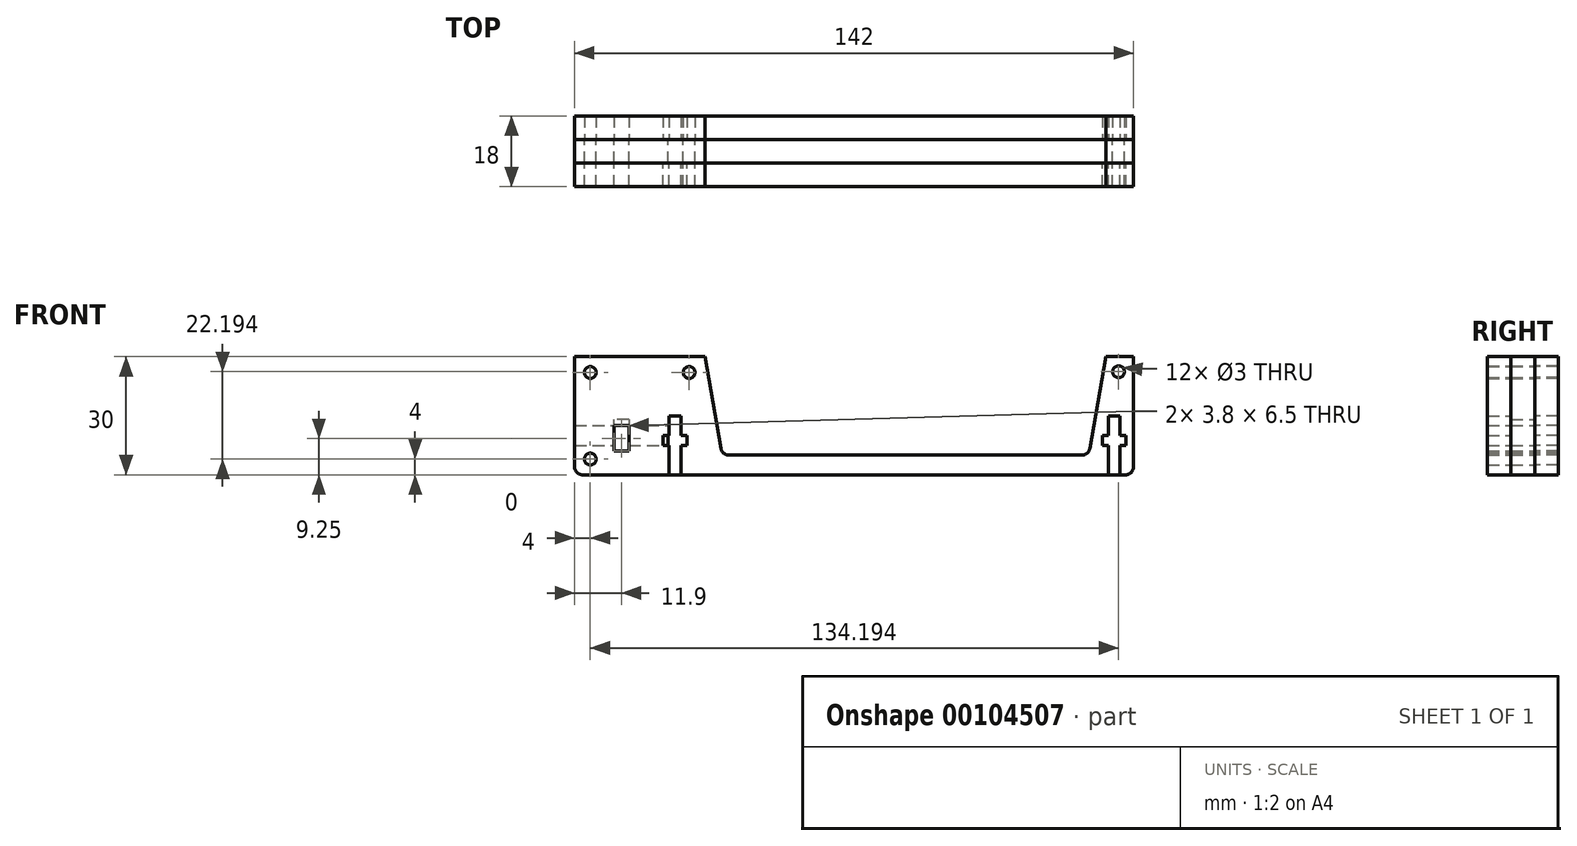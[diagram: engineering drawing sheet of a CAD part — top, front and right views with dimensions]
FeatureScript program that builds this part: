
annotation { "Feature Type Name" : "Feature", "Feature Type Description" : "" }
export const myFeature = defineFeature(function(context is Context, id is Id, definition is map)
    precondition{}
    {
        {
            var Q0;
            Q0=qCreatedBy(makeId("Front.planeOp"),FACE);
            var sketch = newSketch(context, id + "F0", { "sketchPlane" : qUnion([Q0])});
            skLineSegment(sketch, "E0", {"start": v(0, 2) * mm, "end": v(0, 7.5) * mm});
            skLineSegment(sketch, "E1", {"start": v(0, 30) * mm, "end": v(33.1, 30) * mm});
            skLineSegment(sketch, "E2", {"start": v(33.1, 30) * mm, "end": v(37.21, 6.65) * mm});
            skLineSegment(sketch, "E3", {"start": v(39.18, 5) * mm, "end": v(128.91, 5) * mm});
            skLineSegment(sketch, "E4", {"start": v(130.88, 6.65) * mm, "end": v(135, 30) * mm});
            skLineSegment(sketch, "E5", {"start": v(135, 30) * mm, "end": v(142, 30) * mm});
            skLineSegment(sketch, "E6", {"start": v(142, 30) * mm, "end": v(142, 2) * mm});
            skLineSegment(sketch, "E7", {"start": v(140, 0) * mm, "end": v(2, 0) * mm});
            skLineSegment(sketch, "E8", {"start": v(0, 10) * mm, "end": v(142, 10) * mm, "construction": true});
            skLineSegment(sketch, "E9", {"start": v(84.05, 0) * mm, "end": v(84.05, 5) * mm, "construction": true});
            skLineSegment(sketch, "E10.bottom", {"start": v(0, 12.5) * mm, "end": v(10, 12.5) * mm});
            skLineSegment(sketch, "E11.top", {"start": v(13.8, 14) * mm, "end": v(10, 14) * mm});
            skLineSegment(sketch, "E11.right", {"start": v(10, 12.5) * mm, "end": v(10, 14) * mm});
            skLineSegment(sketch, "E12", {"start": v(13.8, 14) * mm, "end": v(13.8, 12.5) * mm});
            skLineSegment(sketch, "E13.MirrorCS", {"start": v(13.8, 6) * mm, "end": v(13.8, 7.5) * mm});
            skLineSegment(sketch, "E14.MirrorCS", {"start": v(13.8, 6) * mm, "end": v(10, 6) * mm});
            skLineSegment(sketch, "E15.MirrorCS", {"start": v(0, 7.5) * mm, "end": v(10, 7.5) * mm});
            skLineSegment(sketch, "E16.MirrorCS", {"start": v(10, 7.5) * mm, "end": v(10, 6) * mm});
            skLineSegment(sketch, "E17.trimOffspring", {"start": v(0, 12.5) * mm, "end": v(0, 30) * mm});
            skLineSegment(sketch, "E18.bottom", {"start": v(13.8, 12.5) * mm, "end": v(23.8, 12.5) * mm});
            skLineSegment(sketch, "E18.top", {"start": v(13.8, 7.5) * mm, "end": v(23.8, 7.5) * mm});
            skLineSegment(sketch, "E18.right", {"start": v(23.8, 12.5) * mm, "end": v(23.8, 7.5) * mm});
            skPoint(sketch, "E19.orphan", {"position": v(13.8, 10) * mm});
            skCircle(sketch, "E20", {"center": v(4, 26) * mm, "radius": 1.5 * mm});
            skLineSegment(sketch, "E21", {"start": v(16.55, 30) * mm, "end": v(16.55, 0) * mm, "construction": true});
            skCircle(sketch, "E22.MirrorC", {"center": v(29.1, 26) * mm, "radius": 1.5 * mm});
            skPoint(sketch, "E23.visualSharp", {"position": v(37.5, 5) * mm});
            skArc(sketch, "E23.filletArc", {"start": v(37.21, 6.65) * mm, "mid": v(37.9, 5.47) * mm, "end": v(39.18, 5) * mm});
            skPoint(sketch, "E24.visualSharp", {"position": v(130.6, 5) * mm});
            skArc(sketch, "E24.filletArc", {"start": v(128.91, 5) * mm, "mid": v(130.2, 5.47) * mm, "end": v(130.88, 6.65) * mm});
            skPoint(sketch, "E25.visualSharp", {"position": v(0, 0) * mm});
            skArc(sketch, "E25.filletArc", {"start": v(0, 2) * mm, "mid": v(0.59, 0.59) * mm, "end": v(2, 0) * mm});
            skPoint(sketch, "E26.visualSharp", {"position": v(142, 0) * mm});
            skArc(sketch, "E26.filletArc", {"start": v(140, 0) * mm, "mid": v(141.41, 0.59) * mm, "end": v(142, 2) * mm});
            skLineSegment(sketch, "E27", {"start": v(34.2, 23.75) * mm, "end": v(133.9, 23.75) * mm, "construction": true});
            skLineSegment(sketch, "E28", {"start": v(0, 15) * mm, "end": v(35.74, 15) * mm, "construction": true});
            skCircle(sketch, "E29.MirrorC", {"center": v(4, 4) * mm, "radius": 1.5 * mm});
            skCircle(sketch, "E30", {"center": v(138.2, 26.2) * mm, "radius": 1.5 * mm});
            skSolve(sketch);
        }
        {
            var Q0;
            Q0=makeQuery(id+"F0.imprint","IMPRINT",FACE,{"disambiguationData":[TD([[makeQuery(id+"F0.imprint","IMPRINT",EDGE,{"derivedFrom":sQuery(id+"F0.wireOp",EDGE,"E0")}),-1.0]])]});
            extrude(context, id + "F1", {"entities" : qUnion([Q0]), "endBound" : BoundingType.SYMMETRIC, "depth" : 6 * mm});
        }
        {
            var Q0;
            Q0=makeQuery(id+"F1.opExtrude","CAP_FACE",FACE,{"disambiguationData":[OSD([sQuery(id+"F0.wireOp",EDGE,"E0"),sQuery(id+"F0.wireOp",EDGE,"E1"),sQuery(id+"F0.wireOp",EDGE,"E2"),sQuery(id+"F0.wireOp",EDGE,"E3"),sQuery(id+"F0.wireOp",EDGE,"E4"),sQuery(id+"F0.wireOp",EDGE,"E5"),sQuery(id+"F0.wireOp",EDGE,"E6"),sQuery(id+"F0.wireOp",EDGE,"E7"),sQuery(id+"F0.wireOp",EDGE,"E10.bottom"),sQuery(id+"F0.wireOp",EDGE,"E11.top"),sQuery(id+"F0.wireOp",EDGE,"E11.right"),sQuery(id+"F0.wireOp",EDGE,"E12"),sQuery(id+"F0.wireOp",EDGE,"E13.MirrorCS"),sQuery(id+"F0.wireOp",EDGE,"E14.MirrorCS"),sQuery(id+"F0.wireOp",EDGE,"E15.MirrorCS"),sQuery(id+"F0.wireOp",EDGE,"E16.MirrorCS"),sQuery(id+"F0.wireOp",EDGE,"E17.trimOffspring"),sQuery(id+"F0.wireOp",EDGE,"E18.bottom"),sQuery(id+"F0.wireOp",EDGE,"E18.top"),sQuery(id+"F0.wireOp",EDGE,"E18.right"),sQuery(id+"F0.wireOp",EDGE,"E20"),sQuery(id+"F0.wireOp",EDGE,"E22.MirrorC"),sQuery(id+"F0.wireOp",EDGE,"E23.filletArc"),sQuery(id+"F0.wireOp",EDGE,"E24.filletArc"),sQuery(id+"F0.wireOp",EDGE,"E25.filletArc"),sQuery(id+"F0.wireOp",EDGE,"E26.filletArc"),sQuery(id+"F0.wireOp",EDGE,"7ebb5a96-6937-4616-b541-9366bf32e80d0.MirrorC"),sQuery(id+"F0.wireOp",EDGE,"E29.MirrorC")])],"isStart":false});
            var sketch = newSketch(context, id + "F2", { "sketchPlane" : qUnion([Q0])});
            skLineSegment(sketch, "E31.0", {"start": v(0, 30) * mm, "end": v(33.1, 30) * mm});
            skLineSegment(sketch, "E32.0", {"start": v(135.6, 0) * mm, "end": v(27, 0) * mm});
            skArc(sketch, "E33.0", {"start": v(0, 2) * mm, "mid": v(0.59, 0.59) * mm, "end": v(2, 0) * mm});
            skLineSegment(sketch, "E34.0", {"start": v(33.1, 30) * mm, "end": v(37.21, 6.65) * mm});
            skArc(sketch, "E35.0", {"start": v(37.21, 6.65) * mm, "mid": v(37.9, 5.47) * mm, "end": v(39.18, 5) * mm});
            skLineSegment(sketch, "E36.0", {"start": v(39.18, 5) * mm, "end": v(128.91, 5) * mm});
            skArc(sketch, "E37.0", {"start": v(128.91, 5) * mm, "mid": v(130.2, 5.47) * mm, "end": v(130.88, 6.65) * mm});
            skLineSegment(sketch, "E38.0", {"start": v(130.88, 6.65) * mm, "end": v(135, 30) * mm});
            skLineSegment(sketch, "E39.0", {"start": v(135, 30) * mm, "end": v(142, 30) * mm});
            skLineSegment(sketch, "E40.0", {"start": v(142, 30) * mm, "end": v(142, 2) * mm});
            skCircle(sketch, "E41.0", {"center": v(29.1, 26) * mm, "radius": 1.5 * mm});
            skCircle(sketch, "E42.0", {"center": v(4, 26) * mm, "radius": 1.5 * mm});
            skCircle(sketch, "E43.0", {"center": v(4, 4) * mm, "radius": 1.5 * mm});
            skPoint(sketch, "E44.0", {"position": v(10, 12.5) * mm});
            skPoint(sketch, "E45.0", {"position": v(13.8, 12.5) * mm});
            skPoint(sketch, "E46.0", {"position": v(13.8, 7.5) * mm});
            skPoint(sketch, "E47.0", {"position": v(10, 7.5) * mm});
            skLineSegment(sketch, "E48", {"start": v(0, 30) * mm, "end": v(0, 2) * mm});
            skLineSegment(sketch, "E49", {"start": v(10, 12.5) * mm, "end": v(13.8, 12.5) * mm});
            skLineSegment(sketch, "E50", {"start": v(13.8, 7.5) * mm, "end": v(13.8, 12.5) * mm});
            skLineSegment(sketch, "E51", {"start": v(13.8, 7.5) * mm, "end": v(10, 7.5) * mm});
            skLineSegment(sketch, "E52", {"start": v(10, 12.5) * mm, "end": v(10, 7.5) * mm});
            skLineSegment(sketch, "E53.top", {"start": v(27, 15) * mm, "end": v(24, 15) * mm});
            skLineSegment(sketch, "E53.left", {"start": v(27, 0) * mm, "end": v(27, 7.5) * mm});
            skLineSegment(sketch, "E53.right", {"start": v(24, 0) * mm, "end": v(24, 7.5) * mm});
            skLineSegment(sketch, "E54", {"start": v(25.5, 30) * mm, "end": v(25.5, 0) * mm, "construction": true});
            skLineSegment(sketch, "E55", {"start": v(37.21, 6.65) * mm, "end": v(13.8, 6.65) * mm, "construction": true});
            skPoint(sketch, "E56", {"position": v(25.5, 6.65) * mm});
            skLineSegment(sketch, "E57.trimOffspring", {"start": v(24, 0) * mm, "end": v(2, 0) * mm});
            skPoint(sketch, "E58.oppositeSnap0", {"position": v(27, 7.5) * mm});
            skLineSegment(sketch, "E58.bottom", {"start": v(22.5, 10) * mm, "end": v(24, 10) * mm});
            skLineSegment(sketch, "E58.top", {"start": v(22.5, 7.5) * mm, "end": v(24, 7.5) * mm});
            skLineSegment(sketch, "E58.left", {"start": v(22.5, 10) * mm, "end": v(22.5, 7.5) * mm});
            skLineSegment(sketch, "E58.right", {"start": v(28.5, 10) * mm, "end": v(28.5, 7.5) * mm});
            skLineSegment(sketch, "E59.trimOffspring", {"start": v(27, 10) * mm, "end": v(28.5, 10) * mm});
            skLineSegment(sketch, "E60.trimOffspring", {"start": v(24, 10) * mm, "end": v(24, 15) * mm});
            skLineSegment(sketch, "E61.trimOffspring", {"start": v(27, 7.5) * mm, "end": v(28.5, 7.5) * mm});
            skLineSegment(sketch, "E62.trimOffspring", {"start": v(27, 10) * mm, "end": v(27, 15) * mm});
            skCircle(sketch, "E63.0", {"center": v(138.2, 26.2) * mm, "radius": 1.5 * mm});
            skLineSegment(sketch, "E64.1.0.0", {"start": v(135.6, 0) * mm, "end": v(135.6, 7.5) * mm});
            skLineSegment(sketch, "E64.1.0.1", {"start": v(138.6, 0) * mm, "end": v(138.6, 7.5) * mm});
            skLineSegment(sketch, "E64.1.0.2", {"start": v(138.6, 7.5) * mm, "end": v(140.1, 7.5) * mm});
            skLineSegment(sketch, "E64.1.0.3", {"start": v(140.1, 10) * mm, "end": v(140.1, 7.5) * mm});
            skLineSegment(sketch, "E64.1.0.4", {"start": v(138.6, 10) * mm, "end": v(140.1, 10) * mm});
            skLineSegment(sketch, "E64.1.0.5", {"start": v(138.6, 10) * mm, "end": v(138.6, 15) * mm});
            skLineSegment(sketch, "E64.1.0.6", {"start": v(135.6, 10) * mm, "end": v(135.6, 15) * mm});
            skLineSegment(sketch, "E64.1.0.7", {"start": v(134.1, 10) * mm, "end": v(135.6, 10) * mm});
            skLineSegment(sketch, "E64.1.0.8", {"start": v(134.1, 10) * mm, "end": v(134.1, 7.5) * mm});
            skLineSegment(sketch, "E64.1.0.9", {"start": v(134.1, 7.5) * mm, "end": v(135.6, 7.5) * mm});
            skLineSegment(sketch, "E64.1.0.10", {"start": v(138.6, 15) * mm, "end": v(135.6, 15) * mm});
            skLineSegment(sketch, "E64.direction1", {"start": v(24, 0) * mm, "end": v(135.6, 0) * mm, "construction": true});
            skLineSegment(sketch, "E65", {"start": v(142, 2) * mm, "end": v(142, 2) * mm});
            skLineSegment(sketch, "E66", {"start": v(140, 0) * mm, "end": v(138.6, 0) * mm});
            skPoint(sketch, "E67.visualSharp", {"position": v(142, 0) * mm});
            skArc(sketch, "E67.filletArc", {"start": v(140, 0) * mm, "mid": v(141.41, 0.59) * mm, "end": v(142, 2) * mm});
            skPoint(sketch, "E68.orphan", {"position": v(140, 0) * mm});
            skSolve(sketch);
        }
        {
            var Q0;
            {var subQ3=sQuery(id+"F2.wireOp",EDGE,"E31.0");Q0=makeQuery(id+"F2.imprint","IMPRINT",FACE,{"disambiguationData":[TD([[makeQuery(id+"F2.imprint","IMPRINT",EDGE,{"derivedFrom":subQ3}),-1.0]])]});}
            var Q1;
            Q1=makeQuery(id+"F2.imprint","IMPRINT",FACE,{"disambiguationData":[TD([[makeQuery(id+"F2.imprint","IMPRINT",EDGE,{"derivedFrom":sQuery(id+"F2.wireOp",EDGE,"E52")}),-1.0]])]});
            var Q2;
            Q2=makeQuery(id+"F2.imprint","IMPRINT",FACE,{"disambiguationData":[TD([[makeQuery(id+"F2.imprint","IMPRINT",EDGE,{"derivedFrom":sQuery(id+"F2.wireOp",EDGE,"E49")}),1.0]])]});
            var Q3;
            Q3=makeQuery(id+"F2.imprint","IMPRINT",FACE,{"disambiguationData":[TD([[makeQuery(id+"F2.imprint","IMPRINT",EDGE,{"derivedFrom":sQuery(id+"F2.wireOp",EDGE,"E50")}),-1.0]])]});
            var Q4;
            {var subQ2=sQuery(id+"F2.wireOp",EDGE,"E33.0");Q4=makeQuery(id+"F2.imprint","IMPRINT",FACE,{"disambiguationData":[TD([[makeQuery(id+"F2.imprint","IMPRINT",EDGE,{"derivedFrom":subQ2}),1.0]])]});}
            extrude(context, id + "F3", {"entities" : qUnion([Q0, Q1, Q2, Q3, Q4]), "depth" : 6 * mm});
        }
        {
            var Q0;
            Q0=makeQuery(id+"F3.opExtrude","SWEPT_BODY",BODY,{"disambiguationData":[OSD([sQuery(id+"F0.wireOp",EDGE,"E13.MirrorCS"),sQuery(id+"F0.wireOp",EDGE,"E14.MirrorCS"),sQuery(id+"F0.wireOp",EDGE,"E16.MirrorCS"),sQuery(id+"F2.wireOp",EDGE,"E31.0"),sQuery(id+"F2.wireOp",EDGE,"E32.0"),sQuery(id+"F2.wireOp",EDGE,"E33.0"),sQuery(id+"F2.wireOp",EDGE,"E34.0"),sQuery(id+"F2.wireOp",EDGE,"E35.0"),sQuery(id+"F2.wireOp",EDGE,"E36.0"),sQuery(id+"F2.wireOp",EDGE,"E37.0"),sQuery(id+"F2.wireOp",EDGE,"E38.0"),sQuery(id+"F2.wireOp",EDGE,"E39.0"),sQuery(id+"F2.wireOp",EDGE,"E40.0"),sQuery(id+"F2.wireOp",EDGE,"4b5e63bc-1f68-4028-bfeb-d0ec7ad10ee8.0"),sQuery(id+"F2.wireOp",EDGE,"E41.0"),sQuery(id+"F2.wireOp",EDGE,"E42.0"),sQuery(id+"F2.wireOp",EDGE,"E43.0"),sQuery(id+"F2.wireOp",EDGE,"e01fc42a-a1de-4d8d-820e-6a417e50549f.0"),sQuery(id+"F2.wireOp",EDGE,"E48"),sQuery(id+"F2.wireOp",EDGE,"E49"),sQuery(id+"F2.wireOp",EDGE,"E50"),sQuery(id+"F2.wireOp",EDGE,"E52")])]});
            var Q1;
            Q1=qCreatedBy(makeId("Front.planeOp"),FACE);
            mirror(context, id + "F4", {"entities" : qUnion([Q0]), "mirrorPlane" : qUnion([Q1])});
        }
    });
